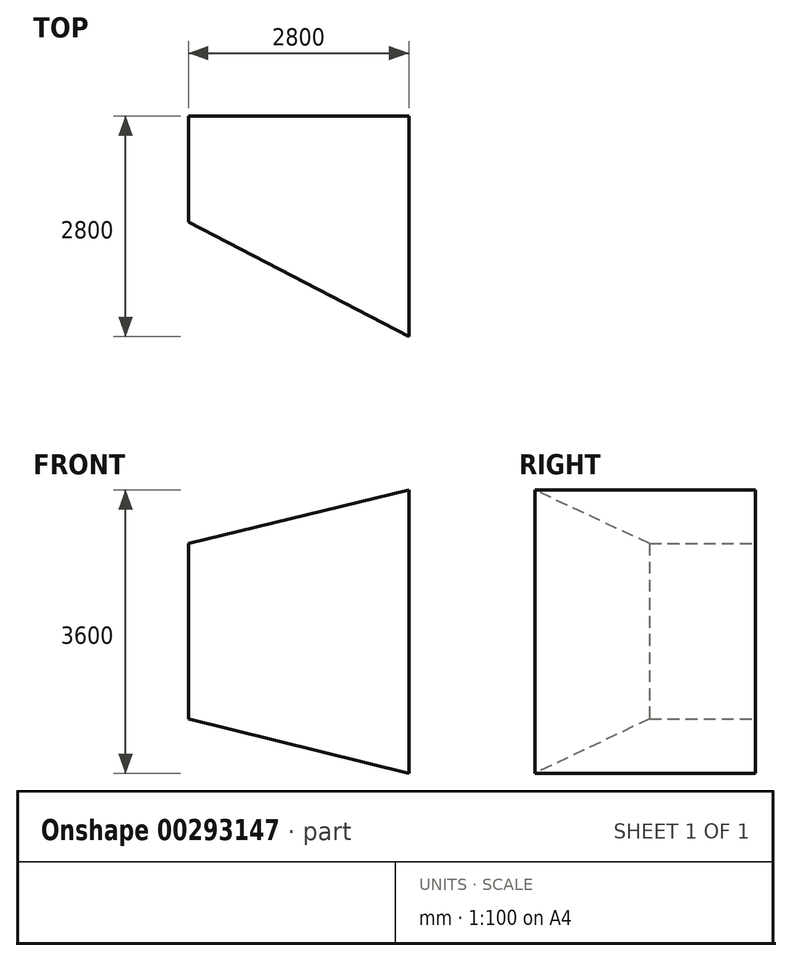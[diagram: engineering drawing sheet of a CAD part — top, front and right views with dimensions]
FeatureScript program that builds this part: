
annotation { "Feature Type Name" : "Feature", "Feature Type Description" : "" }
export const myFeature = defineFeature(function(context is Context, id is Id, definition is map)
    precondition{}
    {
        {
            var Q0;
            Q0=qCreatedBy(makeId("Front.planeOp"),FACE);
            var sketch = newSketch(context, id + "F0", { "sketchPlane" : qUnion([Q0])});
            skLineSegment(sketch, "E0.bottom", {"start": v(-1414.68, 2693.8) * mm, "end": v(1385.32, 2693.8) * mm});
            skLineSegment(sketch, "E0.top", {"start": v(-1414.68, -906.2) * mm, "end": v(1385.32, -906.2) * mm});
            skLineSegment(sketch, "E0.left", {"start": v(-1414.68, 2693.8) * mm, "end": v(-1414.68, -906.2) * mm});
            skLineSegment(sketch, "E0.right", {"start": v(1385.32, 2693.8) * mm, "end": v(1385.32, -906.2) * mm});
            skSolve(sketch);
        }
        {
            var Q0;
            Q0=makeQuery(id+"F0.imprint","IMPRINT",FACE,{"disambiguationData":[TD([[makeQuery(id+"F0.imprint","IMPRINT",EDGE,{"derivedFrom":sQuery(id+"F0.wireOp",EDGE,"E0.bottom")}),-1.0]])]});
            extrude(context, id + "F1", {"entities" : qUnion([Q0]), "depth" : 2800 * mm});
        }
        {
            var Q0;
            Q0=makeQuery(id+"F1.opExtrude","CAP_FACE",FACE,{"disambiguationData":[OSD([sQuery(id+"F0.wireOp",EDGE,"E0.bottom"),sQuery(id+"F0.wireOp",EDGE,"E0.top"),sQuery(id+"F0.wireOp",EDGE,"E0.left"),sQuery(id+"F0.wireOp",EDGE,"E0.right")])],"isStart":true});
            var sketch = newSketch(context, id + "F2", { "sketchPlane" : qUnion([Q0])});
            skLineSegment(sketch, "E1", {"start": v(-1385.32, 2693.8) * mm, "end": v(1414.68, 2012.8) * mm});
            skLineSegment(sketch, "E2", {"start": v(1414.68, 2012.8) * mm, "end": v(1414.68, 2693.8) * mm});
            skLineSegment(sketch, "E3", {"start": v(1414.68, 2693.8) * mm, "end": v(-1385.32, 2693.8) * mm});
            skSolve(sketch);
        }
        {
            var Q0;
            Q0=makeQuery(id+"F2.imprint","IMPRINT",FACE,{"disambiguationData":[TD([[makeQuery(id+"F2.imprint","IMPRINT",EDGE,{"derivedFrom":sQuery(id+"F2.wireOp",EDGE,"E1")}),1.0]])]});
            extrude(context, id + "F3", {"entities" : qUnion([Q0]), "operationType" : NewBodyOperationType.REMOVE, "endBound" : BoundingType.UP_TO_NEXT, "oppositeDirection" : true, "depth" : 2800 * mm});
        }
        {
            var Q0;
            Q0=makeQuery(id+"F1.opExtrude","SWEPT_FACE",FACE,{"disambiguationData":[OSD([sQuery(id+"F0.wireOp",EDGE,"E0.top")])]});
            var sketch = newSketch(context, id + "F4", { "sketchPlane" : qUnion([Q0])});
            skLineSegment(sketch, "E4", {"start": v(-1414.68, 2800) * mm, "end": v(1385.32, 2800) * mm});
            skLineSegment(sketch, "E5", {"start": v(1385.32, 2800) * mm, "end": v(-1414.68, 1344) * mm});
            skLineSegment(sketch, "E6", {"start": v(-1414.68, 1344) * mm, "end": v(-1414.68, 2800) * mm});
            skSolve(sketch);
        }
        {
            var Q0;
            Q0=makeQuery(id+"F4.imprint","IMPRINT",FACE,{"disambiguationData":[TD([[makeQuery(id+"F4.imprint","IMPRINT",EDGE,{"derivedFrom":sQuery(id+"F4.wireOp",EDGE,"E4")}),-1.0]])]});
            extrude(context, id + "F5", {"entities" : qUnion([Q0]), "operationType" : NewBodyOperationType.REMOVE, "endBound" : BoundingType.UP_TO_NEXT, "oppositeDirection" : true, "depth" : 25 * mm});
        }
        {
            var Q0;
            Q0=makeQuery(id+"F1.opExtrude","CAP_FACE",FACE,{"disambiguationData":[OSD([sQuery(id+"F0.wireOp",EDGE,"E0.bottom"),sQuery(id+"F0.wireOp",EDGE,"E0.top"),sQuery(id+"F0.wireOp",EDGE,"E0.left"),sQuery(id+"F0.wireOp",EDGE,"E0.right")])],"isStart":true});
            var sketch = newSketch(context, id + "F6", { "sketchPlane" : qUnion([Q0])});
            skLineSegment(sketch, "E7", {"start": v(1414.68, -906.2) * mm, "end": v(-1385.32, -906.2) * mm});
            skLineSegment(sketch, "E8", {"start": v(-1385.32, -906.2) * mm, "end": v(1414.68, -213.2) * mm});
            skLineSegment(sketch, "E9", {"start": v(1414.68, -213.2) * mm, "end": v(1414.68, -906.2) * mm});
            skSolve(sketch);
        }
        {
            var Q0;
            Q0=makeQuery(id+"F6.imprint","IMPRINT",FACE,{"disambiguationData":[TD([[makeQuery(id+"F6.imprint","IMPRINT",EDGE,{"derivedFrom":sQuery(id+"F6.wireOp",EDGE,"E7")}),-1.0]])]});
            extrude(context, id + "F7", {"entities" : qUnion([Q0]), "operationType" : NewBodyOperationType.REMOVE, "oppositeDirection" : true, "depth" : 2800 * mm});
        }
    });
